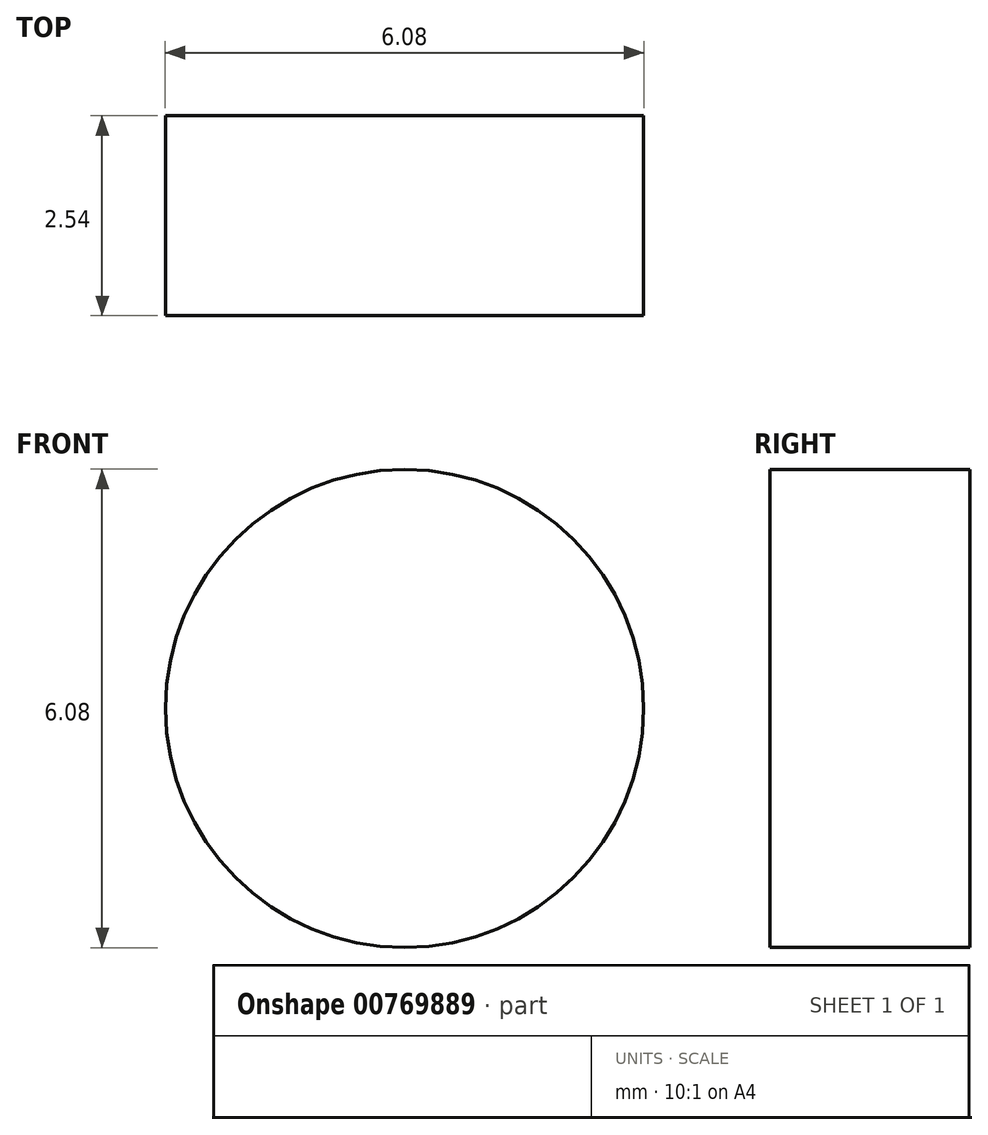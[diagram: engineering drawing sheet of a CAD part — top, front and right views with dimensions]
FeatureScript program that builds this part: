
annotation { "Feature Type Name" : "Feature", "Feature Type Description" : "" }
export const myFeature = defineFeature(function(context is Context, id is Id, definition is map)
    precondition{}
    {
        {
            var Q0;
            Q0=qCreatedBy(makeId("Front.planeOp"),FACE);
            var sketch = newSketch(context, id + "F0", { "sketchPlane" : qUnion([Q0])});
            skCircle(sketch, "E0", {"center": v(0, 0) * mm, "radius": 3.04 * mm});
            skSolve(sketch);
        }
        {
            var Q0;
            Q0 = qSketchRegion(id + "F0", true);
            extrude(context, id + "F1", {"entities" : qUnion([Q0]), "depth" : 2.54 * mm, "offsetDistance" : 25.4 * mm});
        }
    });
